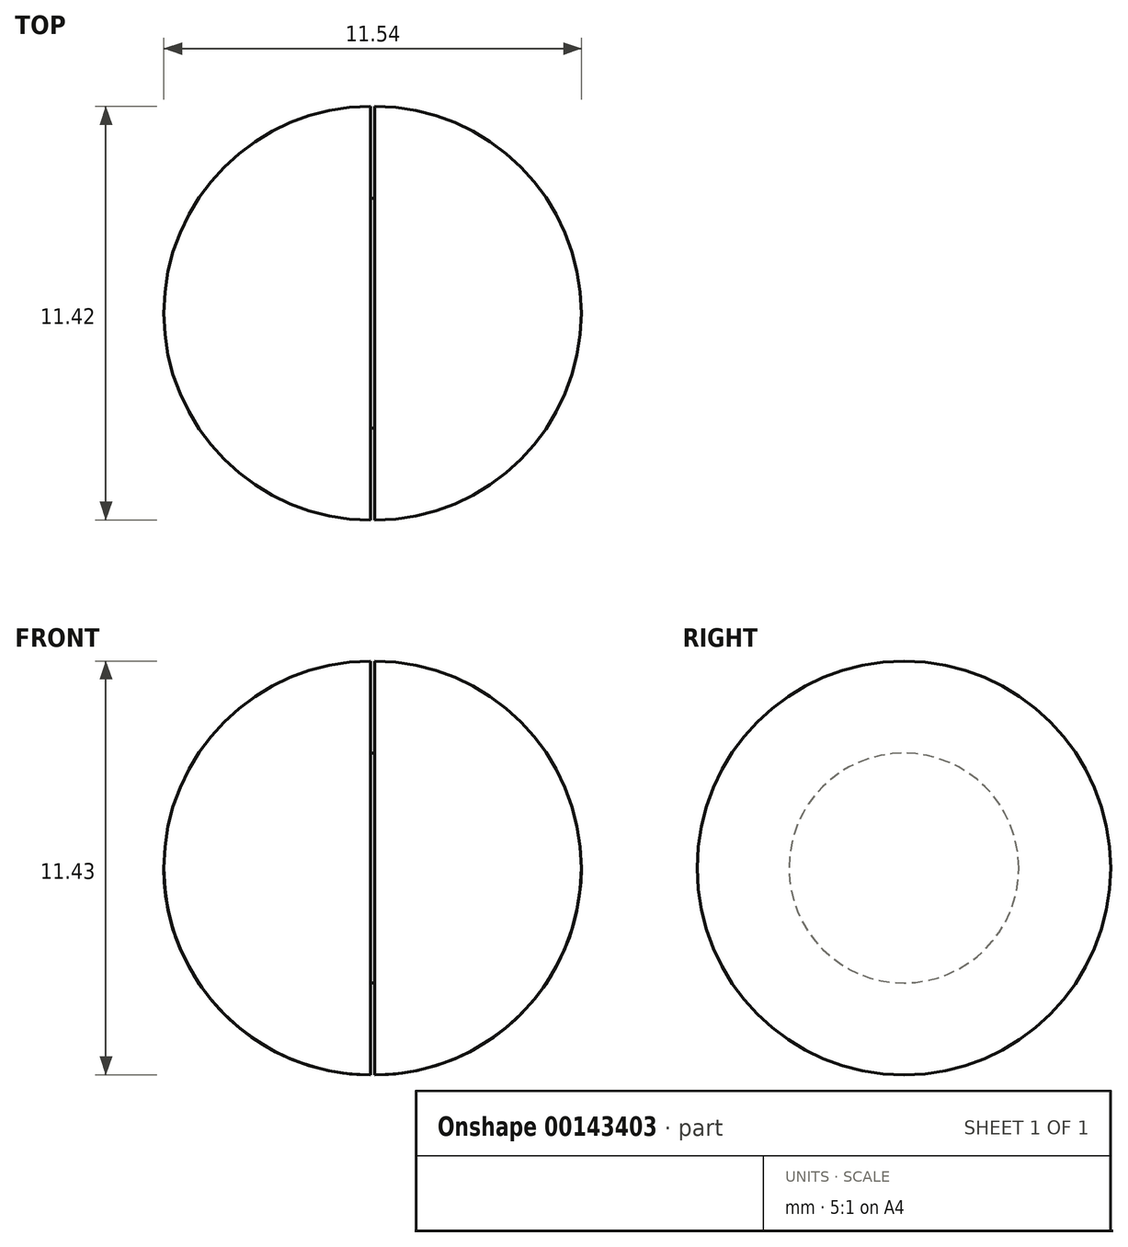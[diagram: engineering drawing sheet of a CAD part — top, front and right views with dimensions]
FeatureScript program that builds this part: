
annotation { "Feature Type Name" : "Feature", "Feature Type Description" : "" }
export const myFeature = defineFeature(function(context is Context, id is Id, definition is map)
    precondition{}
    {
        {
            var Q0;
            Q0=qCreatedBy(makeId("Right.planeOp"),FACE);
            var sketch = newSketch(context, id + "F0", { "sketchPlane" : qUnion([Q0])});
            skCircle(sketch, "E0", {"center": v(0, 0) * mm, "radius": 3.18 * mm});
            skSolve(sketch);
        }
        {
            var Q0;
            Q0=makeQuery(id+"F0.imprint","IMPRINT",FACE,{"disambiguationData":[TD([[makeQuery(id+"F0.imprint","IMPRINT",EDGE,{"derivedFrom":sQuery(id+"F0.wireOp",EDGE,"E0")}),1.0]])]});
            var Q1;
            Q1=qSketchRegion(id+"F2",true);
            extrude(context, id + "F1", {"entities" : qUnion([Q0, Q1]), "oppositeDirection" : true, "depth" : 2.7 / 50.8 * mm});
        }
        {
            var Q0;
            Q0=qCreatedBy(makeId("Front.planeOp"),FACE);
            var sketch = newSketch(context, id + "F2", { "sketchPlane" : qUnion([Q0])});
            skLineSegment(sketch, "E1", {"start": v(0, -3.18) * mm, "end": v(-73.66, -3.18) * mm});
            skLineSegment(sketch, "E2", {"start": v(-73.66, 3.18) * mm, "end": v(0, 3.18) * mm});
            skLineSegment(sketch, "E3", {"start": v(0, 0) * mm, "end": v(0, 5.72) * mm});
            skArc(sketch, "E4", {"start": v(5.72, 0) * mm, "mid": v(4.04, 4.04) * mm, "end": v(0, 5.72) * mm});
            skLineSegment(sketch, "E5", {"start": v(5.72, 0) * mm, "end": v(0, 0) * mm});
            skSolve(sketch);
        }
        {
            var Q0;
            {var subQ3=sQuery(id+"F2.wireOp",EDGE,"E4");Q0=makeQuery(id+"F2.imprint","IMPRINT",FACE,{"disambiguationData":[TD([[makeQuery(id+"F2.imprint","IMPRINT",EDGE,{"derivedFrom":subQ3}),1.0]])]});}
            var Q1;
            Q1=makeQuery(id+"F1.opExtrude","SWEPT_FACE",FACE,{"disambiguationData":[OSD([sQuery(id+"F0.wireOp",EDGE,"E0")])]});
            revolve(context, id + "F3", {"operationType" : NewBodyOperationType.ADD, "entities" : qUnion([Q0]), "axis" : qUnion([Q1]), "revolveType" : RevolveType.FULL});
        }
        {
            var Q0;
            Q0=makeQuery(id+"F1.opExtrude","SWEPT_BODY",BODY,{"disambiguationData":[OSD([sQuery(id+"F0.wireOp",EDGE,"E0")])]});
            var Q1;
            Q1=makeQuery(id+"F1.opExtrude","CAP_FACE",FACE,{"disambiguationData":[OSD([sQuery(id+"F0.wireOp",EDGE,"E0")])],"isStart":false});
            mirror(context, id + "F4", {"operationType" : NewBodyOperationType.ADD, "entities" : qUnion([Q0]), "mirrorPlane" : qUnion([Q1])});
        }
    });
